# Revit family: Kitchen_Soap_Dispenser-American_Standard-4503.115_Series
name_source: partatom
category: Specialty Equipment
revit_build: Autodesk Revit 2014 (Build: 20130308_1515(x64)
units: mm (PartAtom-declared; Revit-internal decimal feet)

## types (3) — shared parameters
Assembly Code = C1030200
Description = Liquid Soap Dispenser
Height = 12 7/8"
Length = 3 1/4"
Manufacturer = American Standard
Product Documentation Link = https://www.americanstandard-us.com
Product URL = https://www.americanstandard-us.com
Specification = Bidet Fitting. Metal Speed Connect Pop-up drain. Swivel spray aerator.
URL = http://www.americanstandard-us.com
Width = 3 1/4"

## per-type parameters (varying)
| type | Finish | Material |
| 4503.115.002 | Metal-American Standard-002-Polished Chrome | Metal-American Standard-002-Polished Chrome |
| 4503.115.075 | Metal-American Standard-075-Stainless steel | Metal-American Standard-075-Stainless steel |
| 4503.115.295 | Metal-American Standard-295-Brushed Nickel | Metal-American Standard-295-Brushed Nickel |

note: column(s) folded — value = type name in every type: Model

## geometry (parser evidence)
native form markers: Sweep x1
no freeform markers — native parametric forms only
